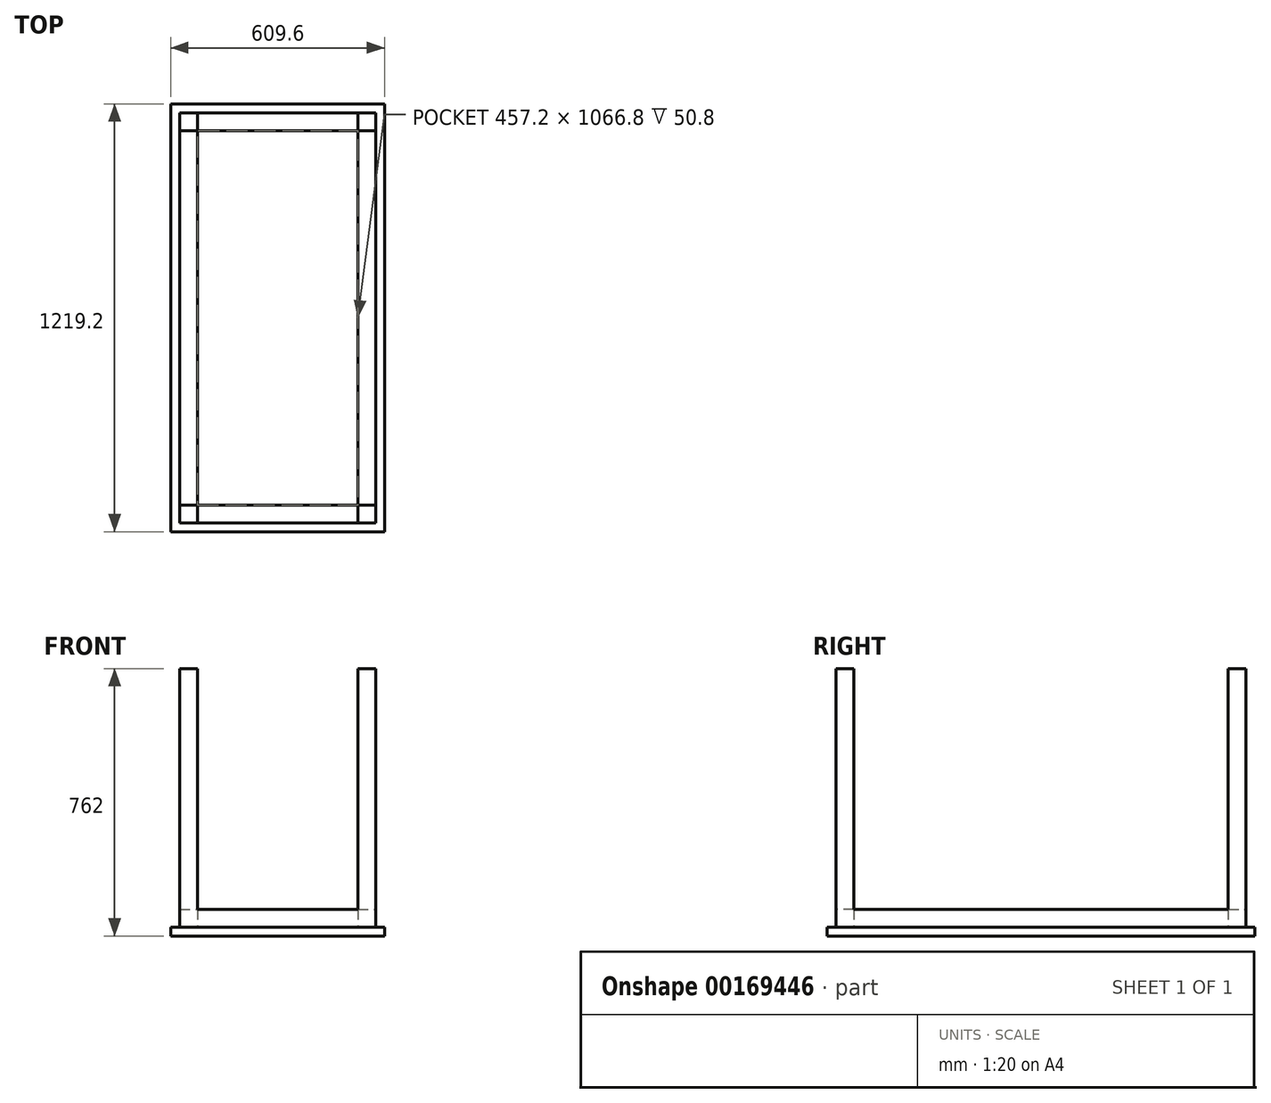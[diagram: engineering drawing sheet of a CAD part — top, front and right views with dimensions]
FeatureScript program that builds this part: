
annotation { "Feature Type Name" : "Feature", "Feature Type Description" : "" }
export const myFeature = defineFeature(function(context is Context, id is Id, definition is map)
    precondition{}
    {
        {
            var Q0;
            Q0=qCreatedBy(makeId("Top.planeOp"),FACE);
            var sketch = newSketch(context, id + "F0", { "sketchPlane" : qUnion([Q0])});
            skLineSegment(sketch, "E0.bottom", {"start": v(-314.86, 594.71) * mm, "end": v(294.74, 594.71) * mm});
            skLineSegment(sketch, "E0.top", {"start": v(-314.86, -624.49) * mm, "end": v(294.74, -624.49) * mm});
            skLineSegment(sketch, "E0.left", {"start": v(-314.86, 594.71) * mm, "end": v(-314.86, -624.49) * mm});
            skLineSegment(sketch, "E0.right", {"start": v(294.74, 594.71) * mm, "end": v(294.74, -624.49) * mm});
            skSolve(sketch);
        }
        {
            var Q0;
            Q0 = qSketchRegion(id + "F0", true);
            extrude(context, id + "F1", {"entities" : qUnion([Q0]), "depth" : 25.4 * mm});
        }
        {
            var Q0;
            Q0=makeQuery(id+"F1.opExtrude","CAP_FACE",FACE,{"disambiguationData":[OSD([sQuery(id+"F0.wireOp",EDGE,"E0.bottom"),sQuery(id+"F0.wireOp",EDGE,"E0.top"),sQuery(id+"F0.wireOp",EDGE,"E0.left"),sQuery(id+"F0.wireOp",EDGE,"E0.right")])],"isStart":false});
            var sketch = newSketch(context, id + "F2", { "sketchPlane" : qUnion([Q0])});
            skLineSegment(sketch, "E1.bottom", {"start": v(-289.46, 569.31) * mm, "end": v(269.34, 569.31) * mm});
            skLineSegment(sketch, "E1.top", {"start": v(-289.46, -599.09) * mm, "end": v(269.34, -599.09) * mm});
            skLineSegment(sketch, "E1.left", {"start": v(-289.46, 569.31) * mm, "end": v(-289.46, -599.09) * mm});
            skLineSegment(sketch, "E1.right", {"start": v(269.34, 569.31) * mm, "end": v(269.34, -599.09) * mm});
            skLineSegment(sketch, "E2.bottom", {"start": v(-238.66, 518.51) * mm, "end": v(218.54, 518.51) * mm});
            skLineSegment(sketch, "E2.top", {"start": v(-238.66, -548.29) * mm, "end": v(218.54, -548.29) * mm});
            skLineSegment(sketch, "E2.left", {"start": v(-238.66, 518.51) * mm, "end": v(-238.66, -548.29) * mm});
            skLineSegment(sketch, "E2.right", {"start": v(218.54, 518.51) * mm, "end": v(218.54, -548.29) * mm});
            skSolve(sketch);
        }
        {
            var Q0;
            Q0 = qSketchRegion(id + "F2", true);
            extrude(context, id + "F3", {"entities" : qUnion([Q0]), "operationType" : NewBodyOperationType.ADD, "depth" : 50.8 * mm});
        }
        {
            var Q0;
            Q0=makeQuery(id+"F3.opExtrude","CAP_FACE",FACE,{"disambiguationData":[OSD([sQuery(id+"F2.wireOp",EDGE,"E1.bottom"),sQuery(id+"F2.wireOp",EDGE,"E1.top"),sQuery(id+"F2.wireOp",EDGE,"E1.left"),sQuery(id+"F2.wireOp",EDGE,"E1.right"),sQuery(id+"F2.wireOp",EDGE,"E2.bottom"),sQuery(id+"F2.wireOp",EDGE,"E2.top"),sQuery(id+"F2.wireOp",EDGE,"E2.left"),sQuery(id+"F2.wireOp",EDGE,"E2.right")])],"isStart":false});
            var sketch = newSketch(context, id + "F4", { "sketchPlane" : qUnion([Q0])});
            skLineSegment(sketch, "E3.bottom", {"start": v(-289.46, 569.31) * mm, "end": v(-238.66, 569.31) * mm});
            skLineSegment(sketch, "E3.top", {"start": v(-289.46, 518.51) * mm, "end": v(-238.66, 518.51) * mm});
            skLineSegment(sketch, "E3.left", {"start": v(-289.46, 569.31) * mm, "end": v(-289.46, 518.51) * mm});
            skLineSegment(sketch, "E3.right", {"start": v(-238.66, 569.31) * mm, "end": v(-238.66, 518.51) * mm});
            skLineSegment(sketch, "E4.bottom", {"start": v(218.54, 518.51) * mm, "end": v(269.34, 518.51) * mm});
            skLineSegment(sketch, "E4.top", {"start": v(218.54, 569.31) * mm, "end": v(269.34, 569.31) * mm});
            skLineSegment(sketch, "E4.left", {"start": v(218.54, 518.51) * mm, "end": v(218.54, 569.31) * mm});
            skLineSegment(sketch, "E4.right", {"start": v(269.34, 518.51) * mm, "end": v(269.34, 569.31) * mm});
            skLineSegment(sketch, "E5.bottom", {"start": v(-289.46, -599.09) * mm, "end": v(-238.66, -599.09) * mm});
            skLineSegment(sketch, "E5.top", {"start": v(-289.46, -548.29) * mm, "end": v(-238.66, -548.29) * mm});
            skLineSegment(sketch, "E5.left", {"start": v(-289.46, -599.09) * mm, "end": v(-289.46, -548.29) * mm});
            skLineSegment(sketch, "E5.right", {"start": v(-238.66, -599.09) * mm, "end": v(-238.66, -548.29) * mm});
            skLineSegment(sketch, "E6.bottom", {"start": v(218.54, -548.29) * mm, "end": v(269.34, -548.29) * mm});
            skLineSegment(sketch, "E6.top", {"start": v(218.54, -599.09) * mm, "end": v(269.34, -599.09) * mm});
            skLineSegment(sketch, "E6.left", {"start": v(218.54, -548.29) * mm, "end": v(218.54, -599.09) * mm});
            skLineSegment(sketch, "E6.right", {"start": v(269.34, -548.29) * mm, "end": v(269.34, -599.09) * mm});
            skSolve(sketch);
        }
        {
            var Q0;
            Q0 = qSketchRegion(id + "F4", true);
            extrude(context, id + "F5", {"entities" : qUnion([Q0]), "operationType" : NewBodyOperationType.ADD, "depth" : 685.8 * mm});
        }
    });
